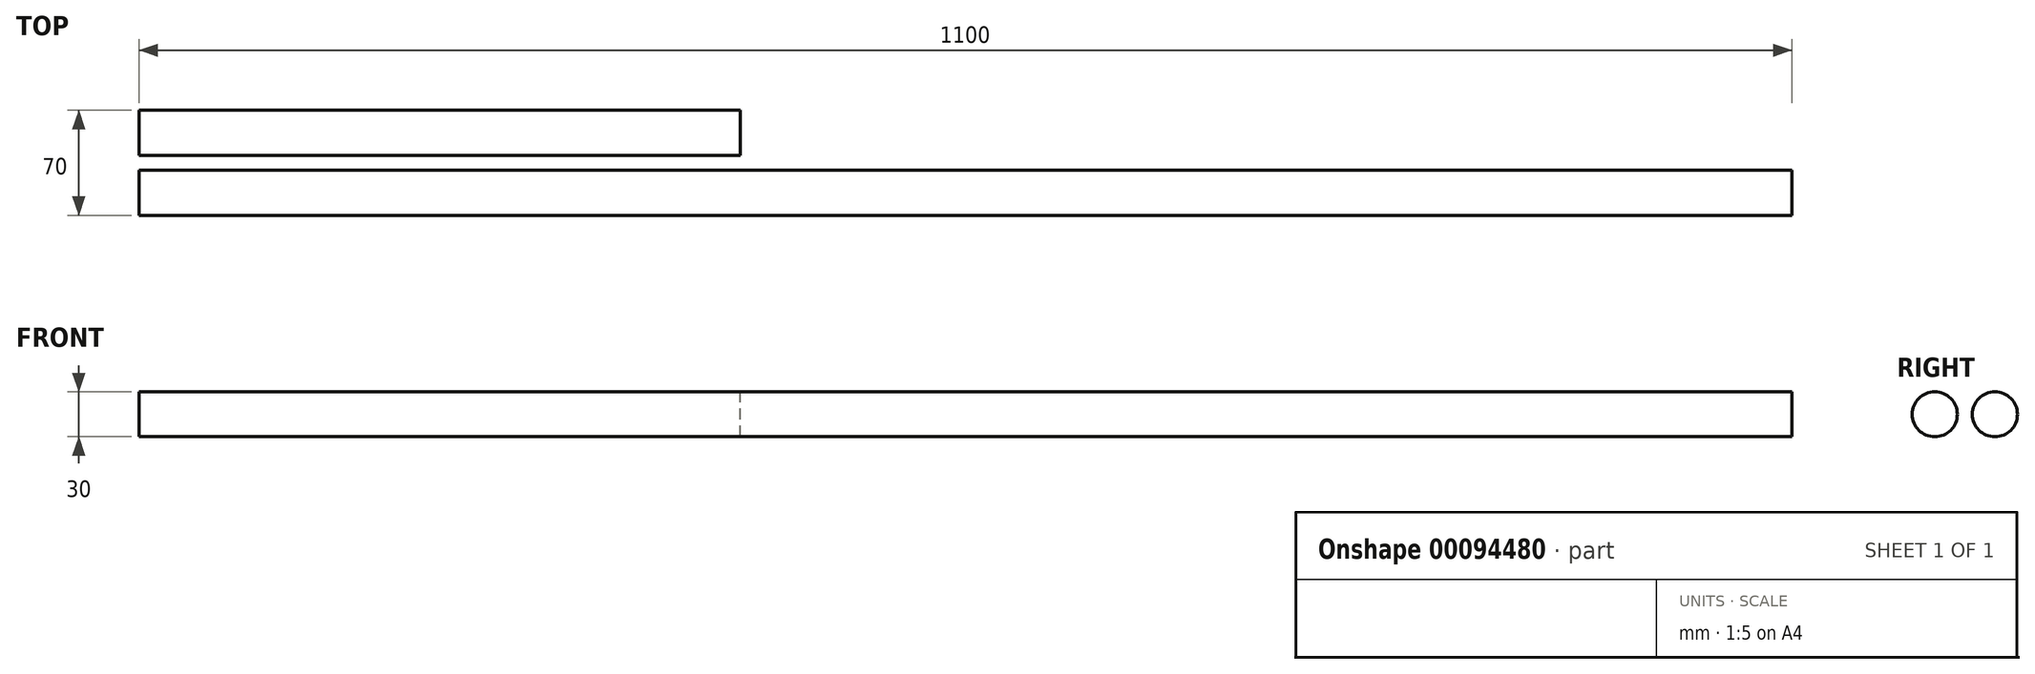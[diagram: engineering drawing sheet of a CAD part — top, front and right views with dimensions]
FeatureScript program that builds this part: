
annotation { "Feature Type Name" : "Feature", "Feature Type Description" : "" }
export const myFeature = defineFeature(function(context is Context, id is Id, definition is map)
    precondition{}
    {
        {
            var Q0;
            Q0=qCreatedBy(makeId("Right.planeOp"),FACE);
            var sketch = newSketch(context, id + "F0", { "sketchPlane" : qUnion([Q0])});
            skCircle(sketch, "E0", {"center": v(0, 0) * mm, "radius": 15 * mm});
            skCircle(sketch, "E1", {"center": v(40, 0) * mm, "radius": 15 * mm});
            skSolve(sketch);
        }
        {
            var Q0;
            Q0=makeQuery(id+"F0.imprint","IMPRINT",FACE,{"disambiguationData":[TD([[makeQuery(id+"F0.imprint","IMPRINT",EDGE,{"derivedFrom":sQuery(id+"F0.wireOp",EDGE,"E0")}),1.0]])]});
            var Q1;
            Q1=makeQuery(id+"F0.imprint","IMPRINT",FACE,{"disambiguationData":[TD([[makeQuery(id+"F0.imprint","IMPRINT",EDGE,{"derivedFrom":sQuery(id+"F0.wireOp",EDGE,"E0")}),1.0]])]});
            extrude(context, id + "F1", {"entities" : qUnion([Q0, Q1]), "depth" : 1100 * mm});
        }
        {
            var Q0;
            Q0 = qSketchRegion(id + "FXAdOBtPfPg6KQTga_1", true);
            var Q1;
            Q1=makeQuery(id+"F0.imprint","IMPRINT",FACE,{"disambiguationData":[TD([[makeQuery(id+"F0.imprint","IMPRINT",EDGE,{"derivedFrom":sQuery(id+"F0.wireOp",EDGE,"E1")}),1.0]])]});
            extrude(context, id + "F2", {"entities" : qUnion([Q0, Q1]), "depth" : 400 * mm});
        }
    });
